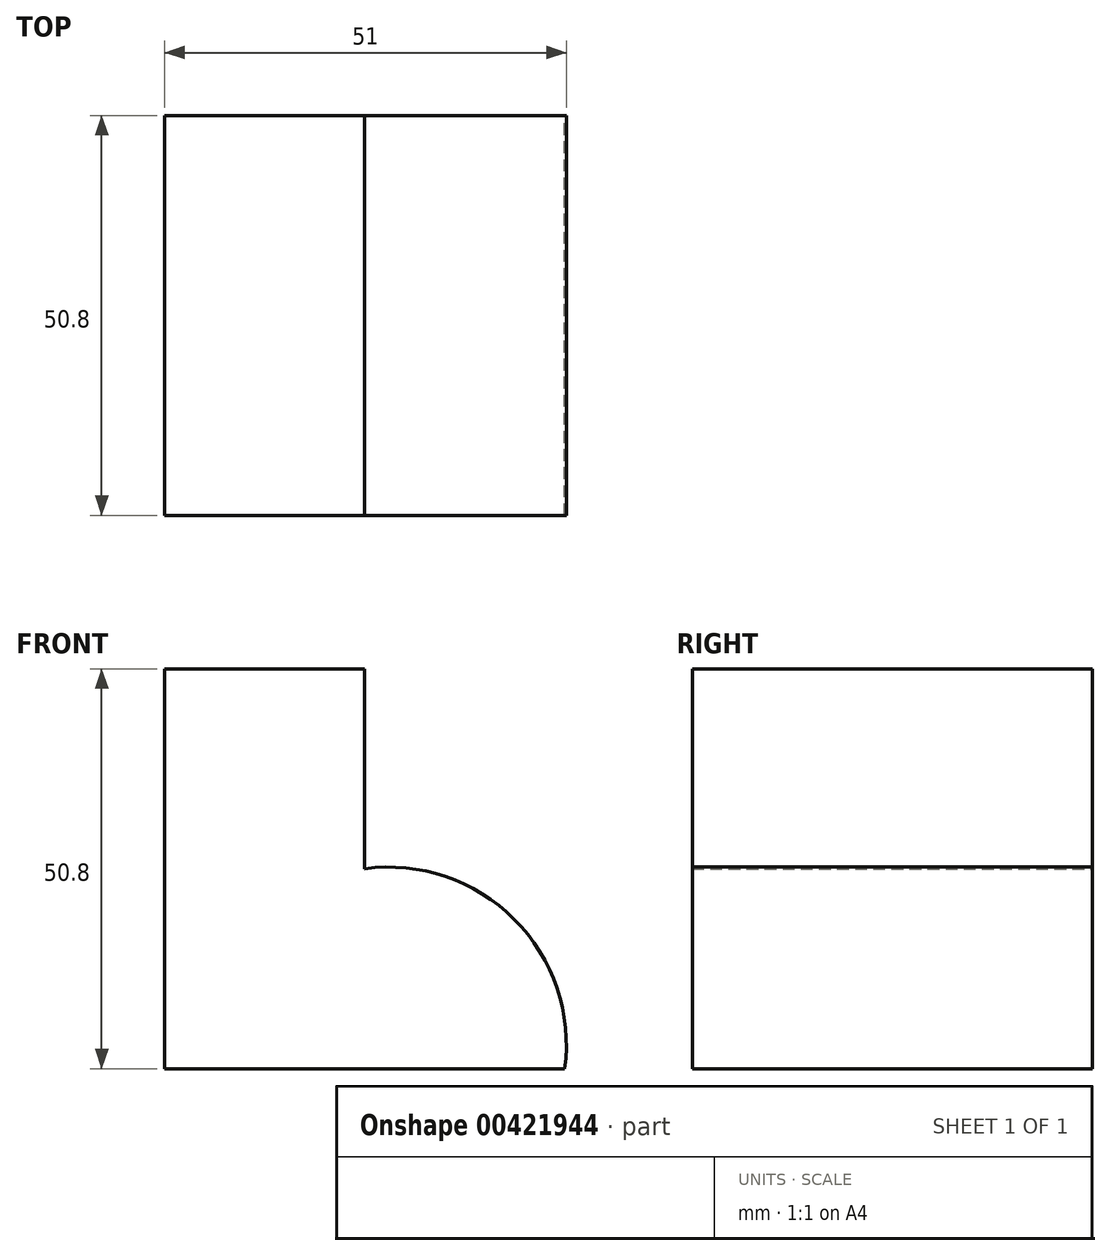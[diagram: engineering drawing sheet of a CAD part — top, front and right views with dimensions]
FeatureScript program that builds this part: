
annotation { "Feature Type Name" : "Feature", "Feature Type Description" : "" }
export const myFeature = defineFeature(function(context is Context, id is Id, definition is map)
    precondition{}
    {
        {
            var Q0;
            Q0=qCreatedBy(makeId("Front.planeOp"),FACE);
            var sketch = newSketch(context, id + "F0", { "sketchPlane" : qUnion([Q0])});
            skLineSegment(sketch, "E0", {"start": v(0, 0) * mm, "end": v(-50.8, 0) * mm});
            skLineSegment(sketch, "E1", {"start": v(-50.8, 0) * mm, "end": v(-50.8, 50.8) * mm});
            skLineSegment(sketch, "E2", {"start": v(-50.8, 50.8) * mm, "end": v(-25.4, 50.8) * mm});
            skLineSegment(sketch, "E3", {"start": v(-25.4, 50.8) * mm, "end": v(-25.4, 25.4) * mm});
            skArc(sketch, "E4", {"start": v(0, 0) * mm, "mid": v(-6.41, 18.99) * mm, "end": v(-25.4, 25.4) * mm});
            skSolve(sketch);
        }
        {
            var Q0;
            Q0 = qSketchRegion(id + "F0", true);
            extrude(context, id + "F1", {"entities" : qUnion([Q0]), "depth" : 50.8 * mm});
        }
    });
